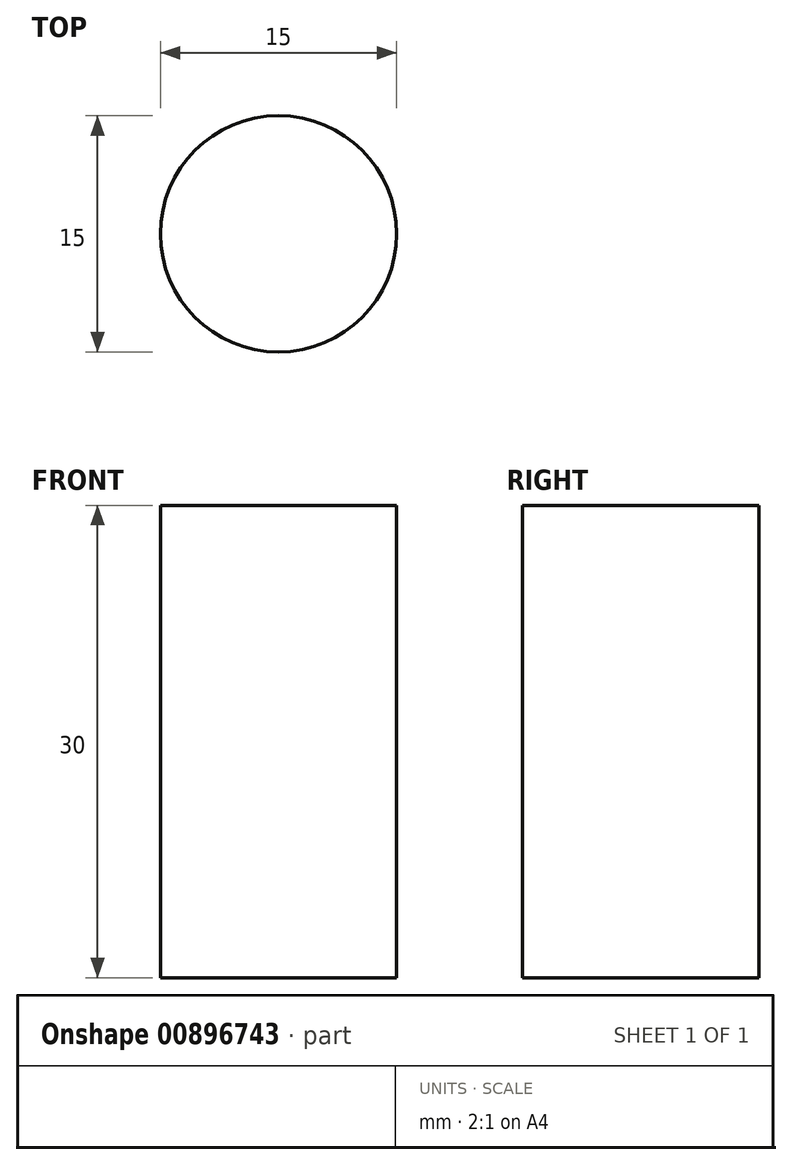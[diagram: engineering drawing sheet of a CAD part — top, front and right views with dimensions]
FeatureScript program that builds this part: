
annotation { "Feature Type Name" : "Feature", "Feature Type Description" : "" }
export const myFeature = defineFeature(function(context is Context, id is Id, definition is map)
    precondition{}
    {
        {
            var Q0;
            Q0=qCreatedBy(makeId("Top.planeOp"),FACE);
            var sketch = newSketch(context, id + "F0", { "sketchPlane" : qUnion([Q0])});
            skCircle(sketch, "E0", {"center": v(0, 0) * mm, "radius": 7.5 * mm});
            skSolve(sketch);
        }
        {
            var Q0;
            Q0=makeQuery(id+"F0.imprint","IMPRINT",FACE,{"disambiguationData":[TD([[makeQuery(id+"F0.imprint","IMPRINT",EDGE,{"derivedFrom":sQuery(id+"F0.wireOp",EDGE,"E0")}),1.0]])]});
            extrude(context, id + "F1", {"entities" : qUnion([Q0]), "depth" : 30 * mm, "offsetDistance" : 25 * mm});
        }
    });
